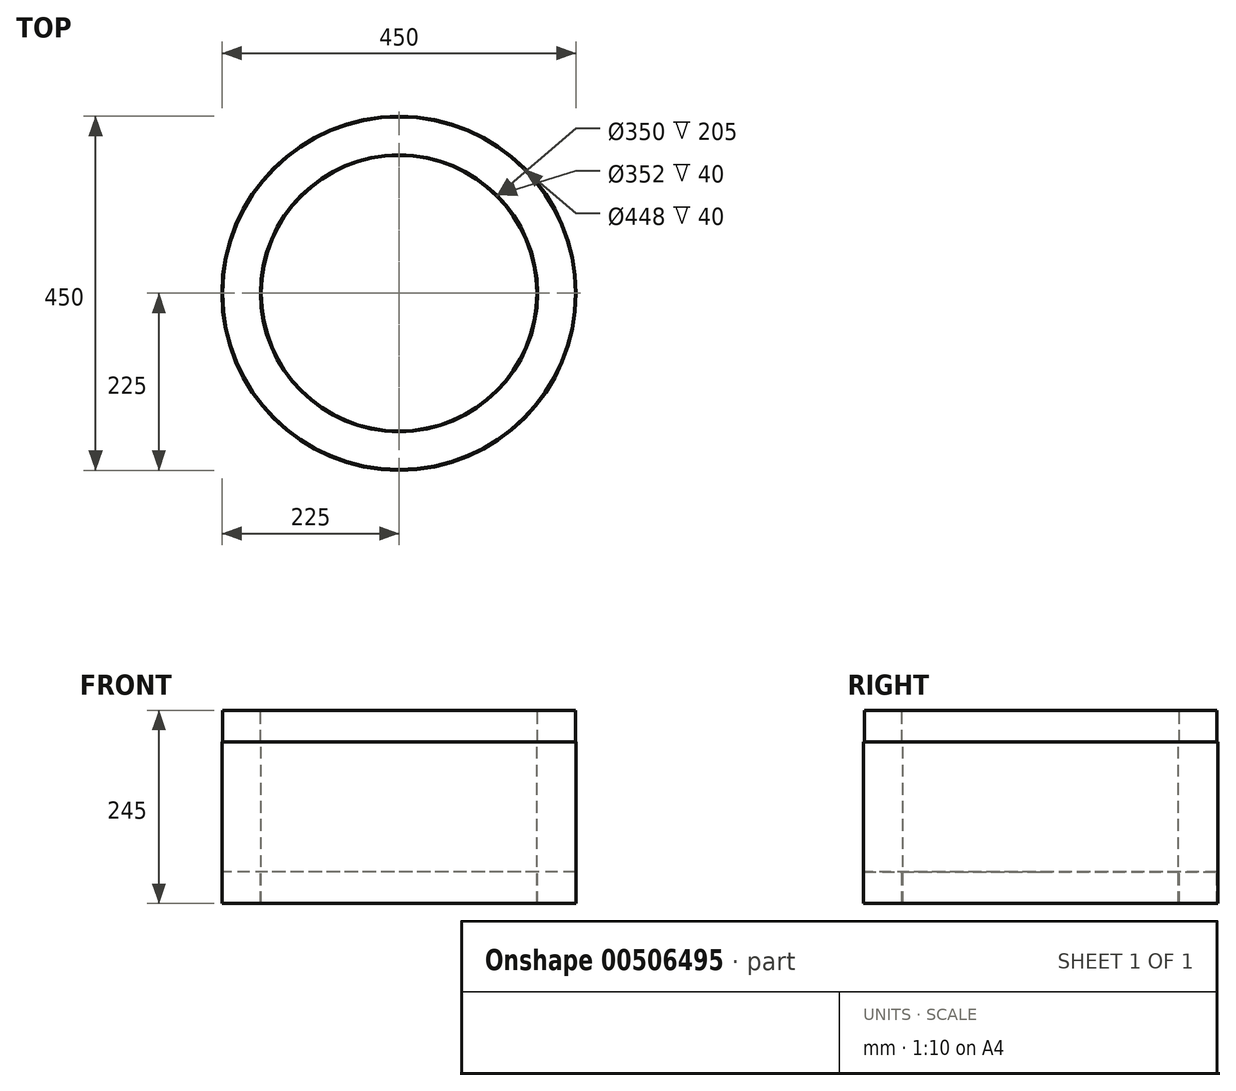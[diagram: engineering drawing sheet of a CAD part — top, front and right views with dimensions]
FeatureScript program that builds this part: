
annotation { "Feature Type Name" : "Feature", "Feature Type Description" : "" }
export const myFeature = defineFeature(function(context is Context, id is Id, definition is map)
    precondition{}
    {
        {
            var Q0;
            Q0=qCreatedBy(makeId("Front.planeOp"),FACE);
            var sketch = newSketch(context, id + "F0", { "sketchPlane" : qUnion([Q0])});
            skLineSegment(sketch, "E0", {"start": v(0, 74.87) * mm, "end": v(0, -73.71) * mm, "construction": true});
            skLineSegment(sketch, "E1", {"start": v(0, 374.84) * mm, "end": v(0, -528.94) * mm, "construction": true});
            skLineSegment(sketch, "E2", {"start": v(-175, -489.75) * mm, "end": v(-175, -284.75) * mm});
            skLineSegment(sketch, "E3", {"start": v(-175, -284.75) * mm, "end": v(-176, -284.75) * mm});
            skLineSegment(sketch, "E4", {"start": v(-176, -284.75) * mm, "end": v(-176, -244.75) * mm});
            skLineSegment(sketch, "E5", {"start": v(-176, -244.75) * mm, "end": v(-224, -244.75) * mm});
            skLineSegment(sketch, "E6", {"start": v(-224, -244.75) * mm, "end": v(-224, -284.75) * mm});
            skLineSegment(sketch, "E7", {"start": v(-224, -284.75) * mm, "end": v(-225, -284.75) * mm});
            skLineSegment(sketch, "E8", {"start": v(-225, -284.75) * mm, "end": v(-225, -489.75) * mm});
            skLineSegment(sketch, "E9", {"start": v(-225, -489.75) * mm, "end": v(-224, -489.75) * mm});
            skLineSegment(sketch, "E10", {"start": v(-224, -489.75) * mm, "end": v(-224, -449.75) * mm});
            skLineSegment(sketch, "E11", {"start": v(-224, -449.75) * mm, "end": v(-176, -449.75) * mm});
            skLineSegment(sketch, "E12", {"start": v(-176, -449.75) * mm, "end": v(-176, -489.75) * mm});
            skLineSegment(sketch, "E13", {"start": v(-176, -489.75) * mm, "end": v(-175, -489.75) * mm});
            skSolve(sketch);
        }
        {
            var Q0;
            Q0=qSketchRegion(id+"F0",true);
            var Q1;
            Q1=sQuery(id+"F0.wireOp",EDGE,"E1");
            revolve(context, id + "F1", {"entities" : qUnion([Q0]), "axis" : qUnion([Q1]), "revolveType" : RevolveType.FULL});
        }
    });
